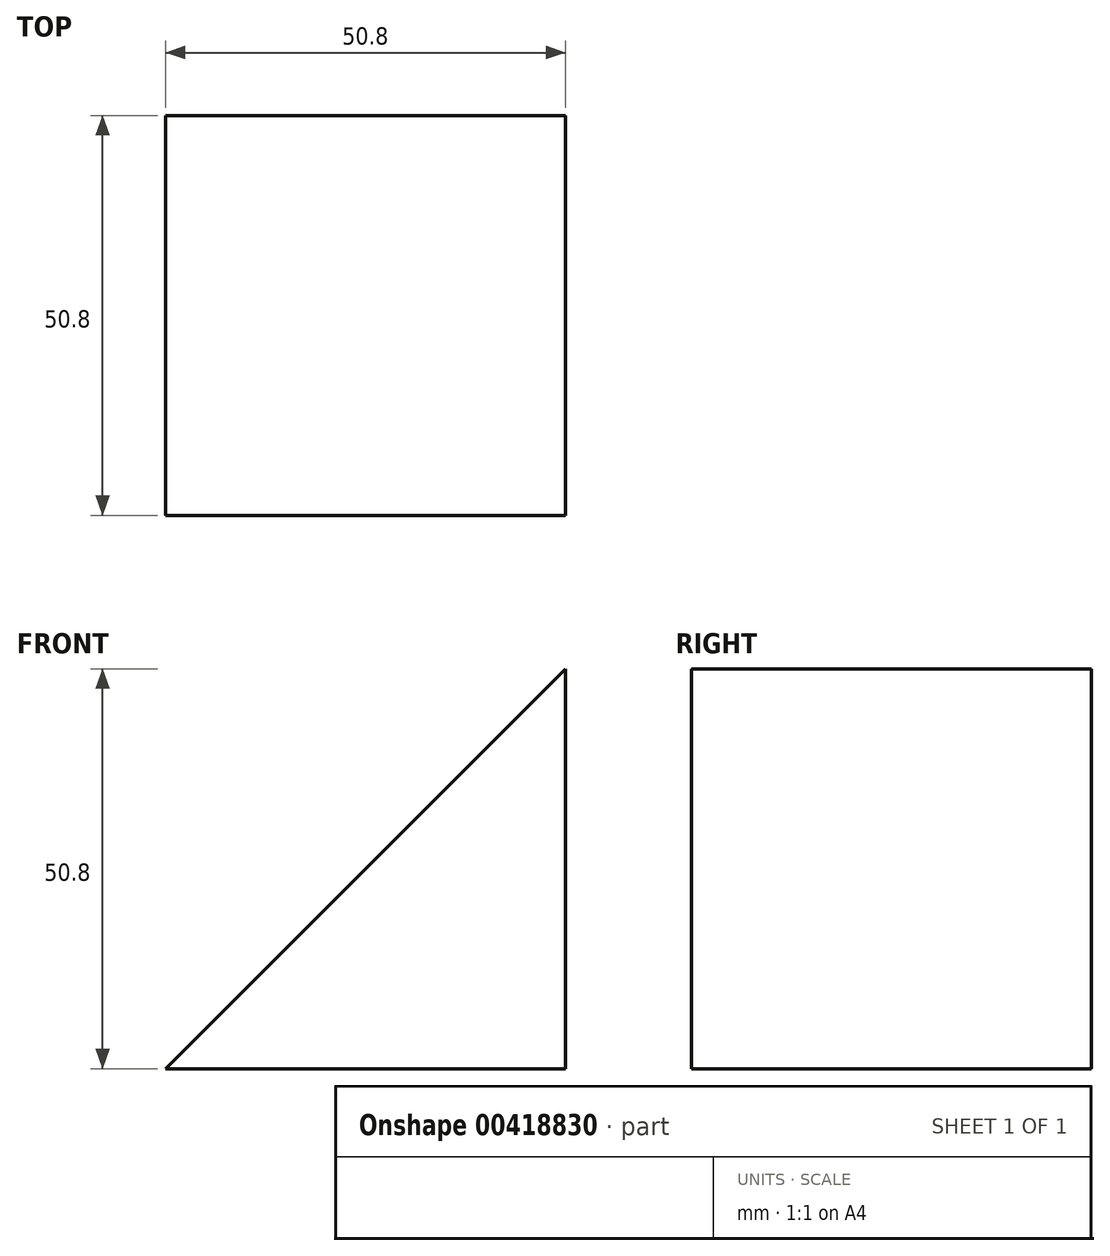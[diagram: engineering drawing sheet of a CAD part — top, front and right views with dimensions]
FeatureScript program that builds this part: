
annotation { "Feature Type Name" : "Feature", "Feature Type Description" : "" }
export const myFeature = defineFeature(function(context is Context, id is Id, definition is map)
    precondition{}
    {
        {
            var Q0;
            Q0=qCreatedBy(makeId("Front.planeOp"),FACE);
            var sketch = newSketch(context, id + "F0", { "sketchPlane" : qUnion([Q0])});
            skLineSegment(sketch, "E0", {"start": v(0, 0) * mm, "end": v(-50.8, 0) * mm});
            skLineSegment(sketch, "E1", {"start": v(0, 0) * mm, "end": v(0, 50.8) * mm});
            skLineSegment(sketch, "E2", {"start": v(0, 50.8) * mm, "end": v(-50.8, 0) * mm});
            skSolve(sketch);
        }
        {
            var Q0;
            Q0=makeQuery(id+"F0.imprint","IMPRINT",FACE,{"disambiguationData":[TD([[makeQuery(id+"F0.imprint","IMPRINT",EDGE,{"derivedFrom":sQuery(id+"F0.wireOp",EDGE,"E0")}),-1.0]])]});
            extrude(context, id + "F1", {"entities" : qUnion([Q0]), "depth" : 50.8 * mm});
        }
    });
